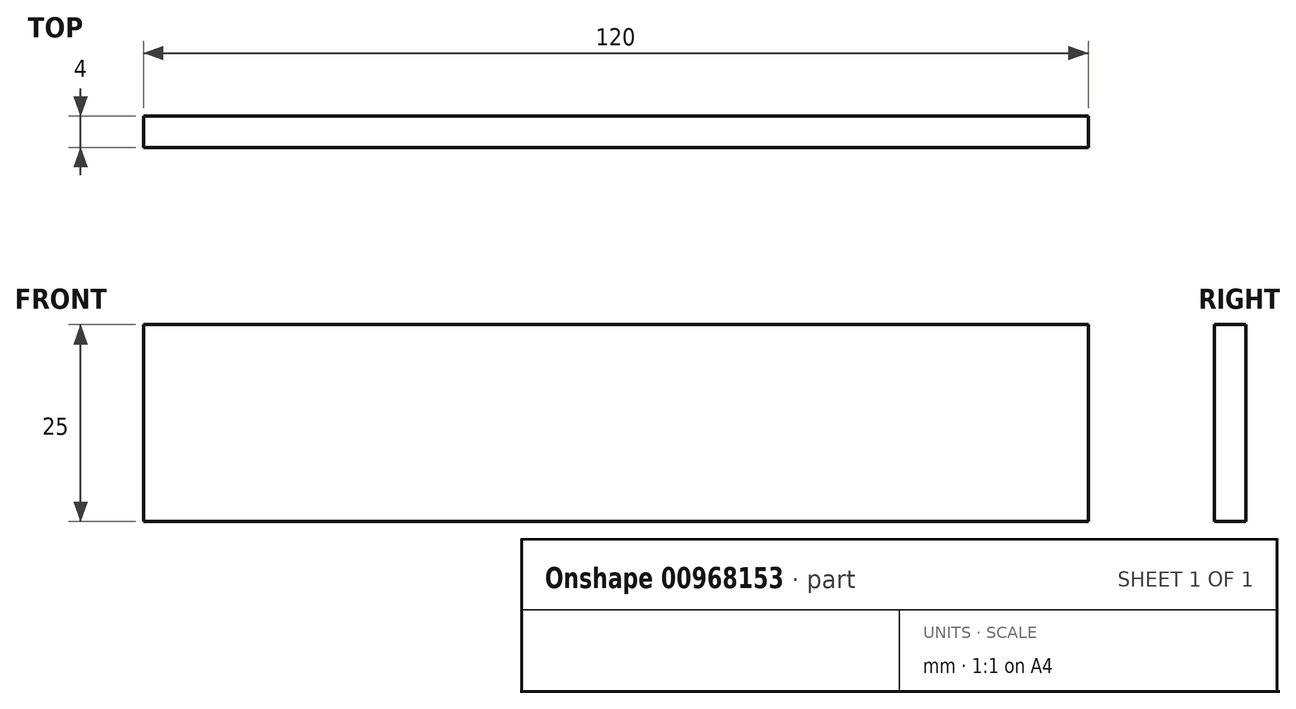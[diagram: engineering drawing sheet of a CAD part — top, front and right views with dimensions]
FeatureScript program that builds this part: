
annotation { "Feature Type Name" : "Feature", "Feature Type Description" : "" }
export const myFeature = defineFeature(function(context is Context, id is Id, definition is map)
    precondition{}
    {
        {
            var Q0;
            Q0=qCreatedBy(makeId("Front.planeOp"),FACE);
            var sketch = newSketch(context, id + "F0", { "sketchPlane" : qUnion([Q0])});
            skLineSegment(sketch, "E0.bottom", {"start": v(60, -12.5) * mm, "end": v(-60, -12.5) * mm});
            skLineSegment(sketch, "E0.top", {"start": v(60, 12.5) * mm, "end": v(-60, 12.5) * mm});
            skLineSegment(sketch, "E0.left", {"start": v(60, -12.5) * mm, "end": v(60, 12.5) * mm});
            skLineSegment(sketch, "E0.right", {"start": v(-60, -12.5) * mm, "end": v(-60, 12.5) * mm});
            skPoint(sketch, "E0.middle", {"position": v(0, 0) * mm});
            skSolve(sketch);
        }
        {
            var Q0;
            Q0=makeQuery(id+"F0.imprint","IMPRINT",FACE,{"disambiguationData":[TD([[makeQuery(id+"F0.imprint","IMPRINT",EDGE,{"derivedFrom":sQuery(id+"F0.wireOp",EDGE,"E0.bottom")}),-1.0]])]});
            extrude(context, id + "F1", {"entities" : qUnion([Q0]), "depth" : 4 * mm, "offsetDistance" : 25 * mm});
        }
    });
